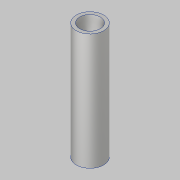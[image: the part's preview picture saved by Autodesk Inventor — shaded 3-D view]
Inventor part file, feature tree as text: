
AUTODESK INVENTOR PART (.ipt)
format: ipt  version: 2019.2 (Build 232265000, 265)  size: 81,408 bytes
history: native  units: mm
features: extrude x1, sketch x1
ambient origin geometry x8: Origin, YZ Plane, XZ Plane, XY Plane, X Axis, Y Axis, Z Axis, Center Point
bodies: Volumenkörper1 (feature_tree)
feature tree (2):
  extrude  "Extrusion1"  Depth=17.0mm
  sketch  "Skizze1"  dims[d3=17.0mm d4=0.0mm d5=0.5mm d6=4.0mm]
